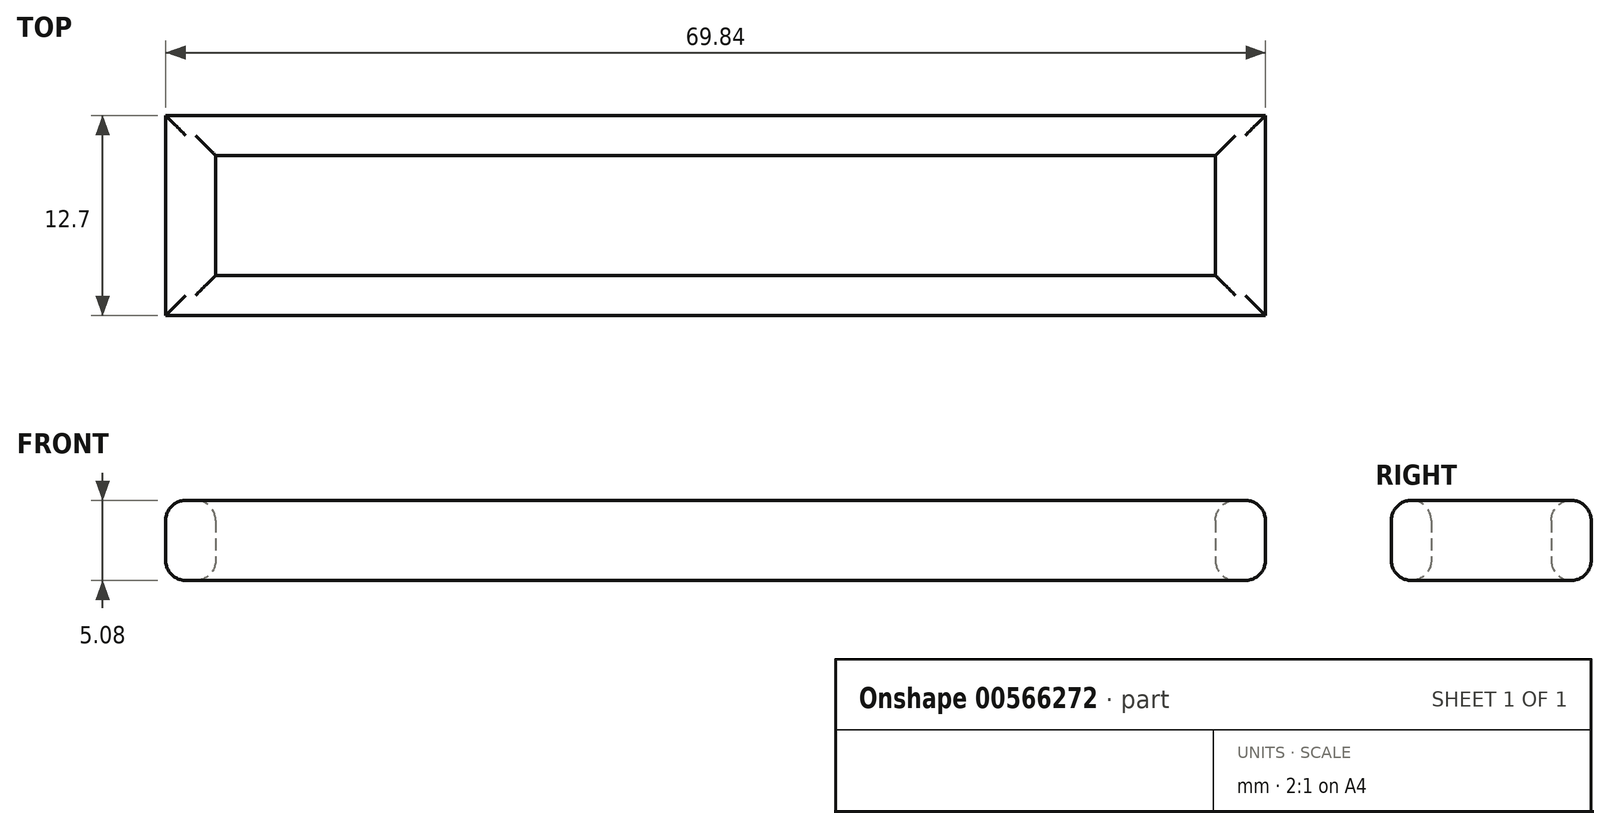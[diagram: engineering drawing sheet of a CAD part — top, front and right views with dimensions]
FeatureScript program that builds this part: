
annotation { "Feature Type Name" : "Feature", "Feature Type Description" : "" }
export const myFeature = defineFeature(function(context is Context, id is Id, definition is map)
    precondition{}
    {
        {
            var Q0;
            Q0=qCreatedBy(makeId("Top.planeOp"),FACE);
            var sketch = newSketch(context, id + "F0", { "sketchPlane" : qUnion([Q0])});
            skLineSegment(sketch, "E0.bottom", {"start": v(-34.93, 6.35) * mm, "end": v(34.93, 6.35) * mm});
            skLineSegment(sketch, "E0.top", {"start": v(-34.93, -6.35) * mm, "end": v(34.93, -6.35) * mm});
            skLineSegment(sketch, "E0.left", {"start": v(-34.93, 6.35) * mm, "end": v(-34.93, -6.35) * mm});
            skLineSegment(sketch, "E0.right", {"start": v(34.93, 6.35) * mm, "end": v(34.93, -6.35) * mm});
            skPoint(sketch, "E0.middle", {"position": v(0, 0) * mm});
            skLineSegment(sketch, "E1.bottom", {"start": v(-31.75, 3.81) * mm, "end": v(31.75, 3.81) * mm});
            skLineSegment(sketch, "E1.top", {"start": v(-31.75, -3.81) * mm, "end": v(31.75, -3.81) * mm});
            skLineSegment(sketch, "E1.left", {"start": v(-31.75, 3.81) * mm, "end": v(-31.75, -3.81) * mm});
            skLineSegment(sketch, "E1.right", {"start": v(31.75, 3.81) * mm, "end": v(31.75, -3.81) * mm});
            skSolve(sketch);
        }
        {
            var Q0;
            Q0=makeQuery(id+"F0.imprint","IMPRINT",FACE,{"disambiguationData":[TD([[makeQuery(id+"F0.imprint","IMPRINT",EDGE,{"derivedFrom":sQuery(id+"F0.wireOp",EDGE,"E0.bottom")}),-1.0]])]});
            extrude(context, id + "F1", {"entities" : qUnion([Q0]), "depth" : 5.08 * mm, "offsetDistance" : 25.4 * mm});
        }
        {
            var Q0;
            Q0=makeQuery(id+"F1.opExtrude","CAP_FACE",FACE,{"disambiguationData":[OSD([sQuery(id+"F0.wireOp",EDGE,"E0.bottom"),sQuery(id+"F0.wireOp",EDGE,"E0.top"),sQuery(id+"F0.wireOp",EDGE,"E0.left"),sQuery(id+"F0.wireOp",EDGE,"E0.right"),sQuery(id+"F0.wireOp",EDGE,"E1.bottom"),sQuery(id+"F0.wireOp",EDGE,"E1.top"),sQuery(id+"F0.wireOp",EDGE,"E1.left"),sQuery(id+"F0.wireOp",EDGE,"E1.right")])],"isStart":false});
            var Q1;
            Q1=makeQuery(id+"F1.opExtrude","CAP_FACE",FACE,{"disambiguationData":[OSD([sQuery(id+"F0.wireOp",EDGE,"E0.bottom"),sQuery(id+"F0.wireOp",EDGE,"E0.top"),sQuery(id+"F0.wireOp",EDGE,"E0.left"),sQuery(id+"F0.wireOp",EDGE,"E0.right"),sQuery(id+"F0.wireOp",EDGE,"E1.bottom"),sQuery(id+"F0.wireOp",EDGE,"E1.top"),sQuery(id+"F0.wireOp",EDGE,"E1.left"),sQuery(id+"F0.wireOp",EDGE,"E1.right")])],"isStart":true});
            fillet(context, id + "F2", {"entities" : qUnion([Q0, Q1]), "radius" : 1.27 * mm, "tangentPropagation" : true, "allowEdgeOverflow" : false});
        }
    });
